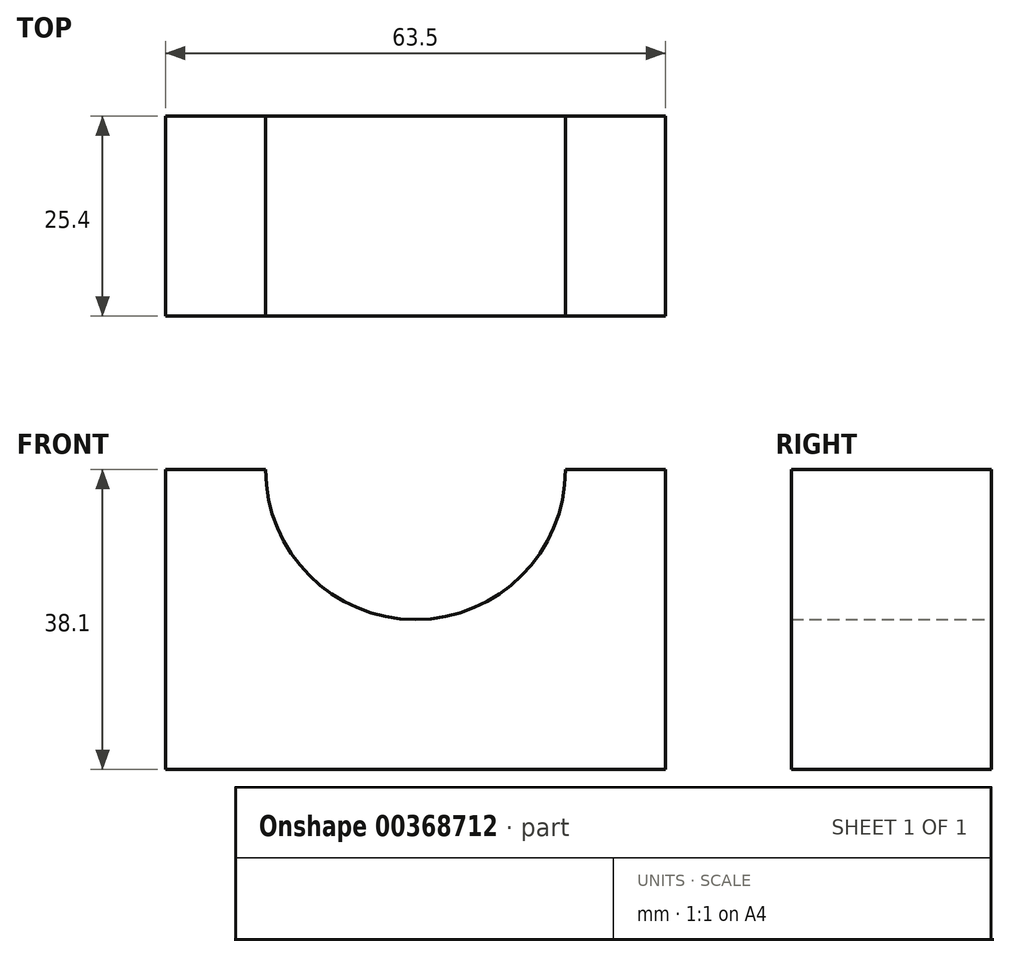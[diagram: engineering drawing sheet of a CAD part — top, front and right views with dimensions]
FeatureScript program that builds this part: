
annotation { "Feature Type Name" : "Feature", "Feature Type Description" : "" }
export const myFeature = defineFeature(function(context is Context, id is Id, definition is map)
    precondition{}
    {
        {
            var Q0;
            Q0=qCreatedBy(makeId("Front.planeOp"),FACE);
            var sketch = newSketch(context, id + "F0", { "sketchPlane" : qUnion([Q0])});
            skLineSegment(sketch, "E0", {"start": v(0, 0) * mm, "end": v(0, 38.1) * mm});
            skLineSegment(sketch, "E1", {"start": v(0, 0) * mm, "end": v(63.5, 0) * mm});
            skLineSegment(sketch, "E2", {"start": v(63.5, 0) * mm, "end": v(63.5, 38.1) * mm});
            skLineSegment(sketch, "E3", {"start": v(63.5, 38.1) * mm, "end": v(50.8, 38.1) * mm});
            skLineSegment(sketch, "E4", {"start": v(0, 38.1) * mm, "end": v(12.7, 38.1) * mm});
            skArc(sketch, "E5", {"start": v(12.7, 38.1) * mm, "mid": v(31.75, 19.05) * mm, "end": v(50.8, 38.1) * mm});
            skSolve(sketch);
        }
        {
            var Q0;
            Q0 = qSketchRegion(id + "F0", true);
            extrude(context, id + "F1", {"entities" : qUnion([Q0]), "depth" : 25.4 * mm});
        }
    });
